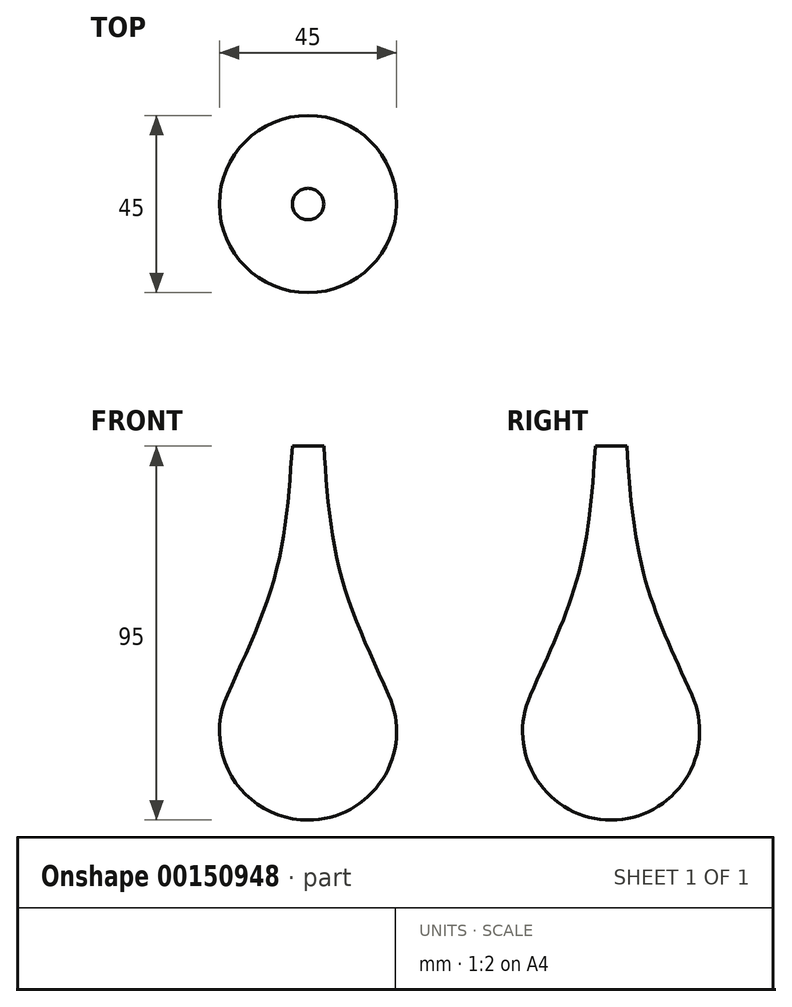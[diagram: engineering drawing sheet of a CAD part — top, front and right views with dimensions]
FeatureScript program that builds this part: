
annotation { "Feature Type Name" : "Feature", "Feature Type Description" : "" }
export const myFeature = defineFeature(function(context is Context, id is Id, definition is map)
    precondition{}
    {
        {
            var Q0;
            Q0=qCreatedBy(makeId("Front.planeOp"),FACE);
            var sketch = newSketch(context, id + "F0", { "sketchPlane" : qUnion([Q0])});
            skArc(sketch, "E0", {"start": v(-20.5, 9.26) * mm, "mid": v(-18.9, -12.2) * mm, "end": v(0, -22.5) * mm});
            skLineSegment(sketch, "E1", {"start": v(0, 72.5) * mm, "end": v(-4, 72.5) * mm});
            skFitSpline(sketch, "E2", {"points": [v(-4, 72.5) * mm, v(-8.15, 40.48) * mm, v(-20.5, 9.26) * mm], "startDerivative": vector(-4.4, -65.4) * mm, "endDerivative": vector(-27.85, -61.67) * mm});
            skLineSegment(sketch, "E3", {"start": v(0, 72.5) * mm, "end": v(0, -22.5) * mm});
            skSolve(sketch);
        }
        {
            var Q0;
            Q0=makeQuery(id+"F0.imprint","IMPRINT",FACE,{"disambiguationData":[TD([[makeQuery(id+"F0.imprint","IMPRINT",EDGE,{"derivedFrom":sQuery(id+"F0.wireOp",EDGE,"E1")}),1.0]])]});
            var Q1;
            {var subQ0=sQuery(id+"F0.wireOp",EDGE,"E0");var subQ1=makeQuery(id+"F0.imprint","INTERSECT",VERTEX,{"derivedFrom":[subQ0,sQuery(id+"F0.wireOp",EDGE,"E2")]});Q1=makeQuery(id+"F0.imprint","IMPRINT",FACE,{"disambiguationData":[TD([[makeQuery(id+"F0.imprint","IMPRINT",EDGE,{"disambiguationData":[TD([[subQ1,1.0]])],"derivedFrom":subQ0}),1.0]])]});}
            var Q2;
            Q2=sQuery(id+"F0.wireOp",EDGE,"E3");
            revolve(context, id + "F1", {"entities" : qUnion([Q0, Q1]), "axis" : qUnion([Q2]), "revolveType" : RevolveType.FULL});
        }
    });
